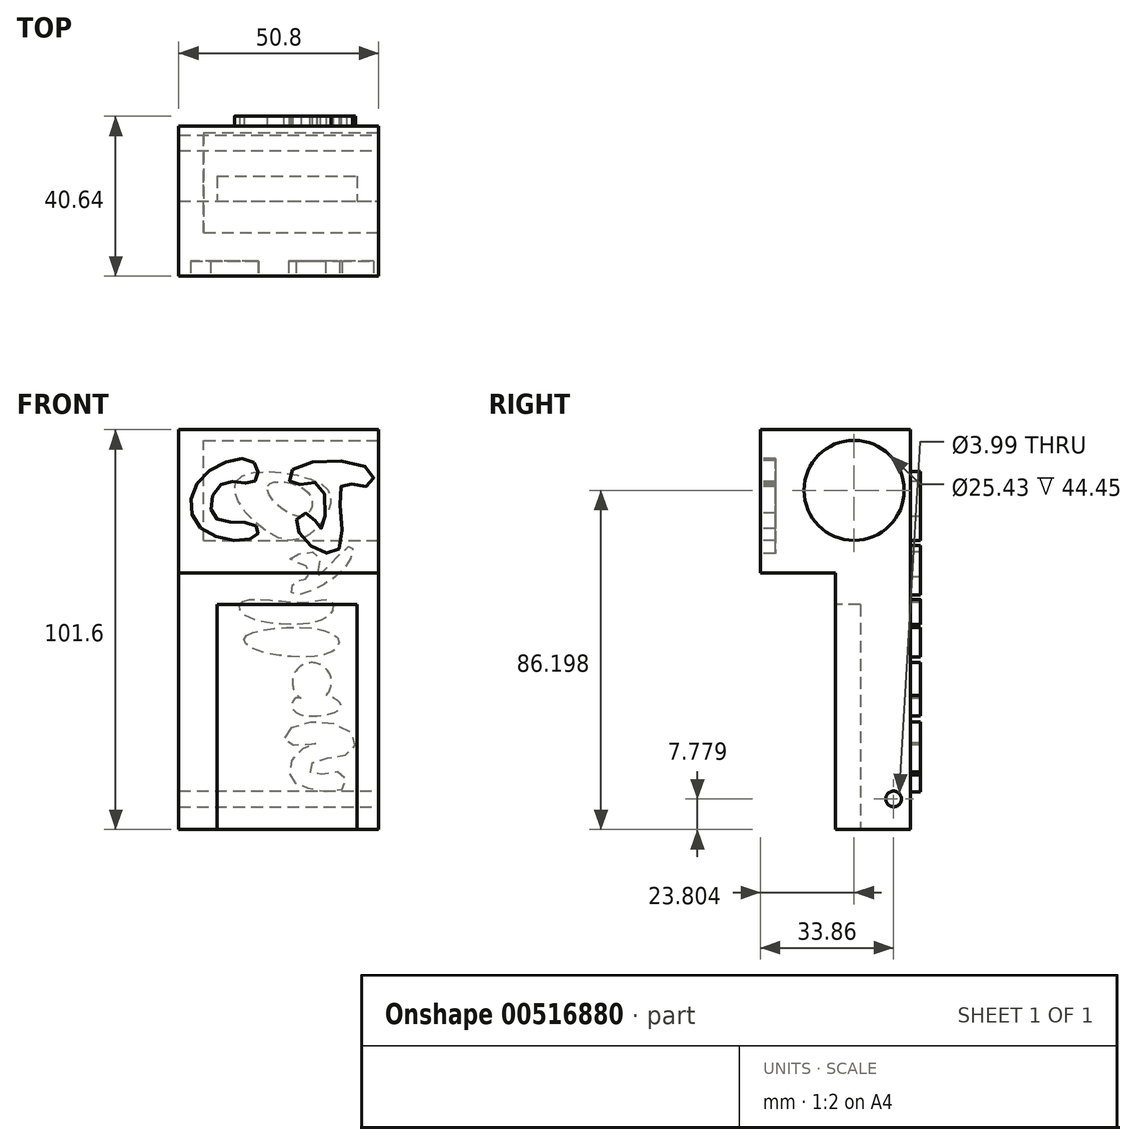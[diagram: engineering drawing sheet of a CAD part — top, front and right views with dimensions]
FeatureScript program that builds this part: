
annotation { "Feature Type Name" : "Feature", "Feature Type Description" : "" }
export const myFeature = defineFeature(function(context is Context, id is Id, definition is map)
    precondition{}
    {
        {
            var Q0;
            Q0=qCreatedBy(makeId("Front.planeOp"),FACE);
            var sketch = newSketch(context, id + "F0", { "sketchPlane" : qUnion([Q0])});
            skLineSegment(sketch, "E0.bottom", {"start": v(-43.59, 59.9) * mm, "end": v(7.21, 59.9) * mm});
            skLineSegment(sketch, "E0.top", {"start": v(-43.59, -41.7) * mm, "end": v(7.21, -41.7) * mm});
            skLineSegment(sketch, "E0.left", {"start": v(-43.59, 59.9) * mm, "end": v(-43.59, -41.7) * mm});
            skLineSegment(sketch, "E0.right", {"start": v(7.21, 59.9) * mm, "end": v(7.21, -41.7) * mm});
            skSolve(sketch);
        }
        {
            var Q0;
            Q0=makeQuery(id+"F0.imprint","IMPRINT",FACE,{"disambiguationData":[TD([[makeQuery(id+"F0.imprint","IMPRINT",EDGE,{"derivedFrom":sQuery(id+"F0.wireOp",EDGE,"E0.bottom")}),-1.0]])]});
            extrude(context, id + "F1", {"entities" : qUnion([Q0]), "depth" : 38.1 * mm, "offsetDistance" : 25.4 * mm});
        }
        {
            var Q0;
            Q0=makeQuery(id+"F1.opExtrude","CAP_FACE",FACE,{"disambiguationData":[OSD([sQuery(id+"F0.wireOp",EDGE,"E0.bottom"),sQuery(id+"F0.wireOp",EDGE,"E0.top"),sQuery(id+"F0.wireOp",EDGE,"E0.left"),sQuery(id+"F0.wireOp",EDGE,"E0.right")])],"isStart":false});
            var sketch = newSketch(context, id + "F2", { "sketchPlane" : qUnion([Q0])});
            skLineSegment(sketch, "E1.bottom", {"start": v(-33.9, 15.45) * mm, "end": v(1.66, 15.45) * mm});
            skLineSegment(sketch, "E1.top", {"start": v(-33.9, -41.7) * mm, "end": v(1.66, -41.7) * mm});
            skLineSegment(sketch, "E1.left", {"start": v(-33.9, 15.45) * mm, "end": v(-33.9, -41.7) * mm});
            skLineSegment(sketch, "E1.right", {"start": v(1.66, 15.45) * mm, "end": v(1.66, -41.7) * mm});
            skSolve(sketch);
        }
        {
            var Q0;
            Q0=makeQuery(id+"F2.imprint","IMPRINT",FACE,{"disambiguationData":[TD([[makeQuery(id+"F2.imprint","IMPRINT",EDGE,{"derivedFrom":sQuery(id+"F2.wireOp",EDGE,"E1.bottom")}),-1.0]])]});
            extrude(context, id + "F3", {"entities" : qUnion([Q0]), "operationType" : NewBodyOperationType.REMOVE, "oppositeDirection" : true, "depth" : 25.4 * mm, "offsetDistance" : 25.4 * mm});
        }
        {
            var Q0;
            Q0=makeQuery(id+"F1.opExtrude","SWEPT_FACE",FACE,{"disambiguationData":[OSD([sQuery(id+"F0.wireOp",EDGE,"E0.right")])]});
            var sketch = newSketch(context, id + "F4", { "sketchPlane" : qUnion([Q0])});
            skCircle(sketch, "E2", {"center": v(-4.24, -33.92) * mm, "radius": 2 * mm});
            skSolve(sketch);
        }
        {
            var Q0;
            Q0=makeQuery(id+"F4.imprint","IMPRINT",FACE,{"disambiguationData":[TD([[makeQuery(id+"F4.imprint","IMPRINT",EDGE,{"derivedFrom":sQuery(id+"F4.wireOp",EDGE,"E2")}),1.0]])]});
            extrude(context, id + "F5", {"entities" : qUnion([Q0]), "operationType" : NewBodyOperationType.REMOVE, "endBound" : BoundingType.THROUGH_ALL, "oppositeDirection" : true, "depth" : 25.4 * mm, "offsetDistance" : 25.4 * mm});
        }
        {
            var Q0;
            Q0=makeQuery(id+"F1.opExtrude","SWEPT_FACE",FACE,{"disambiguationData":[OSD([sQuery(id+"F0.wireOp",EDGE,"E0.right")])]});
            var sketch = newSketch(context, id + "F6", { "sketchPlane" : qUnion([Q0])});
            skCircle(sketch, "E3", {"center": v(-14.3, 44.5) * mm, "radius": 12.71 * mm});
            skSolve(sketch);
        }
        {
            var Q0;
            Q0=makeQuery(id+"F1.opExtrude","CAP_FACE",FACE,{"disambiguationData":[OSD([sQuery(id+"F0.wireOp",EDGE,"E0.bottom"),sQuery(id+"F0.wireOp",EDGE,"E0.top"),sQuery(id+"F0.wireOp",EDGE,"E0.left"),sQuery(id+"F0.wireOp",EDGE,"E0.right")])],"isStart":false});
            var sketch = newSketch(context, id + "F7", { "sketchPlane" : qUnion([Q0])});
            skLineSegment(sketch, "E4", {"start": v(-43.59, 23.47) * mm, "end": v(7.21, 23.47) * mm});
            skSolve(sketch);
        }
        {
            var Q0;
            {var subQ2=sQuery(id+"F7.wireOp",EDGE,"E4");Q0=makeQuery(id+"F7.imprint","IMPRINT",FACE,{"disambiguationData":[TD([[makeQuery(id+"F7.imprint","IMPRINT",EDGE,{"derivedFrom":subQ2}),-1.0]])]});}
            extrude(context, id + "F8", {"entities" : qUnion([Q0]), "operationType" : NewBodyOperationType.REMOVE, "oppositeDirection" : true, "depth" : 19.05 * mm, "offsetDistance" : 25.4 * mm});
        }
        {
            var Q0;
            Q0=makeQuery(id+"F6.imprint","IMPRINT",FACE,{"disambiguationData":[TD([[makeQuery(id+"F6.imprint","IMPRINT",EDGE,{"derivedFrom":sQuery(id+"F6.wireOp",EDGE,"E3")}),1.0]])]});
            extrude(context, id + "F9", {"entities" : qUnion([Q0]), "operationType" : NewBodyOperationType.REMOVE, "oppositeDirection" : true, "depth" : 44.45 * mm, "offsetDistance" : 25.4 * mm});
        }
        {
            var Q0;
            Q0=makeQuery(id+"F1.opExtrude","CAP_FACE",FACE,{"disambiguationData":[OSD([sQuery(id+"F0.wireOp",EDGE,"E0.bottom"),sQuery(id+"F0.wireOp",EDGE,"E0.top"),sQuery(id+"F0.wireOp",EDGE,"E0.left"),sQuery(id+"F0.wireOp",EDGE,"E0.right")])],"isStart":false});
            var sketch = newSketch(context, id + "F10", { "sketchPlane" : qUnion([Q0])});
            skFitSpline(sketch, "E5", {"points": [v(-24.52, 51.62) * mm, v(-37.6, 47.93) * mm, v(-38.16, 35.03) * mm, v(-23.97, 32.82) * mm, v(-24.52, 35.76) * mm, v(-34.66, 37.8) * mm, v(-32.45, 46.27) * mm, v(-24.52, 46.64) * mm, v(-24.52, 51.62) * mm]});
            skFitSpline(sketch, "E6", {"points": [v(-13.27, 49.78) * mm, v(-13.46, 46.46) * mm, v(-6.45, 45.9) * mm, v(-7.74, 35.03) * mm, v(-10.14, 37.8) * mm, v(-13.27, 37.98) * mm, v(-10.88, 30.6) * mm, v(-4.42, 30.79) * mm, v(-1.84, 45.9) * mm, v(4.6, 45.9) * mm, v(4.98, 49.6) * mm, v(-13.27, 49.78) * mm]});
            skSolve(sketch);
        }
        {
            var Q0;
            Q0=makeQuery(id+"F10.imprint","IMPRINT",FACE,{"disambiguationData":[TD([[makeQuery(id+"F10.imprint","IMPRINT",EDGE,{"derivedFrom":sQuery(id+"F10.wireOp",EDGE,"E5")}),1.0]])]});
            extrude(context, id + "F11", {"entities" : qUnion([Q0]), "operationType" : NewBodyOperationType.REMOVE, "oppositeDirection" : true, "depth" : 3.8 * mm, "offsetDistance" : 25.4 * mm});
        }
        {
            var Q0;
            Q0=makeQuery(id+"F1.opExtrude","CAP_FACE",FACE,{"disambiguationData":[OSD([sQuery(id+"F0.wireOp",EDGE,"E0.bottom"),sQuery(id+"F0.wireOp",EDGE,"E0.top"),sQuery(id+"F0.wireOp",EDGE,"E0.left"),sQuery(id+"F0.wireOp",EDGE,"E0.right")])],"isStart":false});
            var sketch = newSketch(context, id + "F12", { "sketchPlane" : qUnion([Q0])});
            skFitSpline(sketch, "E7", {"points": [v(-14.75, 49.78) * mm, v(-14.56, 46.09) * mm, v(-7.56, 45.72) * mm, v(-7.37, 34.84) * mm, v(-10.14, 38.35) * mm, v(-13.64, 37.06) * mm, v(-9.03, 29.68) * mm, v(-2.58, 30.23) * mm, v(-2.03, 45.9) * mm, v(4.24, 45.54) * mm, v(5.16, 49.6) * mm, v(-14.75, 49.78) * mm]});
            skSolve(sketch);
        }
        {
            var Q0;
            Q0=makeQuery(id+"F12.imprint","IMPRINT",FACE,{"disambiguationData":[TD([[makeQuery(id+"F12.imprint","IMPRINT",EDGE,{"derivedFrom":sQuery(id+"F12.wireOp",EDGE,"E7")}),1.0]])]});
            extrude(context, id + "F13", {"entities" : qUnion([Q0]), "operationType" : NewBodyOperationType.REMOVE, "oppositeDirection" : true, "depth" : 3.8 * mm, "offsetDistance" : 25.4 * mm});
        }
        {
            var Q0;
            Q0=makeQuery(id+"F1.opExtrude","CAP_FACE",FACE,{"disambiguationData":[OSD([sQuery(id+"F0.wireOp",EDGE,"E0.bottom"),sQuery(id+"F0.wireOp",EDGE,"E0.top"),sQuery(id+"F0.wireOp",EDGE,"E0.left"),sQuery(id+"F0.wireOp",EDGE,"E0.right")])],"isStart":true});
            var sketch = newSketch(context, id + "F14", { "sketchPlane" : qUnion([Q0])});
            skFitSpline(sketch, "E8", {"points": [v(29.13, 46.64) * mm, v(7.37, 46.09) * mm, v(5.72, 39.08) * mm, v(16.4, 31.9) * mm, v(29.13, 46.64) * mm]});
            skFitSpline(sketch, "E9", {"points": [v(21.02, 45.54) * mm, v(10.5, 43.7) * mm, v(12.54, 37.8) * mm, v(21.02, 45.54) * mm]});
            skFitSpline(sketch, "E10", {"points": [v(15.3, 27.1) * mm, v(8.11, 28.2) * mm, v(8.48, 22.5) * mm, v(0, 30.42) * mm, v(0, 27.1) * mm, v(6.64, 20.65) * mm, v(14.75, 18.25) * mm, v(14.01, 21.2) * mm, v(11.06, 22.12) * mm, v(11.06, 25.07) * mm, v(15.3, 27.1) * mm]});
            skFitSpline(sketch, "E11", {"points": [v(27.28, 16.22) * mm, v(11.43, 16.04) * mm, v(4.98, 16.4) * mm, v(5.72, 12.35) * mm, v(27.1, 12.9) * mm, v(27.28, 16.22) * mm]});
            skFitSpline(sketch, "E12", {"points": [v(26.36, 7.56) * mm, v(4.24, 7.93) * mm, v(4.24, 3.69) * mm, v(25.07, 4.42) * mm, v(26.36, 7.56) * mm]});
            skFitSpline(sketch, "E13", {"points": [v(13.09, -3.32) * mm, v(10.32, 0) * mm, v(5.53, -1.47) * mm, v(6.45, -7.56) * mm, v(11.43, -8.48) * mm, v(13.09, -3.32) * mm]});
            skFitSpline(sketch, "E14", {"points": [v(11.43, -8.48) * mm, v(14.2, -8.48) * mm, v(13.83, -11.98) * mm, v(2.4, -10.7) * mm, v(6.45, -7.56) * mm, v(11.43, -8.48) * mm]});
            skFitSpline(sketch, "E15", {"points": [v(15.12, -15.85) * mm, v(16.22, -19.73) * mm, v(8.48, -19.73) * mm, v(13.27, -21.94) * mm, v(15.3, -28.2) * mm, v(11.43, -30.97) * mm, v(1.66, -31.16) * mm, v(2.21, -27.28) * mm, v(9.59, -27.65) * mm, v(9.59, -24.7) * mm, v(0, -22.12) * mm, v(0, -16.78) * mm, v(15.12, -15.85) * mm]});
            skFitSpline(sketch, "E16", {"points": [v(9.77, -3.5) * mm, v(8.3, -2.21) * mm, v(7.37, -3.32) * mm, v(6.45, -5.53) * mm, v(9.03, -7.56) * mm, v(9.77, -3.5) * mm]});
            skSolve(sketch);
        }
        {
            var Q0;
            Q0=makeQuery(id+"F14.imprint","IMPRINT",FACE,{"disambiguationData":[TD([[makeQuery(id+"F14.imprint","IMPRINT",EDGE,{"derivedFrom":sQuery(id+"F14.wireOp",EDGE,"E8")}),1.0]])]});
            var Q1;
            Q1=makeQuery(id+"F14.imprint","IMPRINT",FACE,{"disambiguationData":[TD([[makeQuery(id+"F14.imprint","IMPRINT",EDGE,{"derivedFrom":sQuery(id+"F14.wireOp",EDGE,"E10")}),1.0]])]});
            var Q2;
            Q2=makeQuery(id+"F14.imprint","IMPRINT",FACE,{"disambiguationData":[TD([[makeQuery(id+"F14.imprint","IMPRINT",EDGE,{"derivedFrom":sQuery(id+"F14.wireOp",EDGE,"E11")}),1.0]])]});
            var Q3;
            Q3=makeQuery(id+"F14.imprint","IMPRINT",FACE,{"disambiguationData":[TD([[makeQuery(id+"F14.imprint","IMPRINT",EDGE,{"derivedFrom":sQuery(id+"F14.wireOp",EDGE,"E12")}),1.0]])]});
            var Q4;
            {var subQ0=sQuery(id+"F14.wireOp",EDGE,"E14");var subQ1=sQuery(id+"F14.wireOp",EDGE,"E13");var subQ2=makeQuery(id+"F14.imprint","INTERSECT",VERTEX,{"disambiguationData":[OD(0.0)],"derivedFrom":[subQ1,subQ0]});Q4=makeQuery(id+"F14.imprint","IMPRINT",FACE,{"disambiguationData":[TD([[makeQuery(id+"F14.imprint","IMPRINT",EDGE,{"disambiguationData":[TD([[subQ2,1.0]])],"derivedFrom":subQ1}),-1.0]])]});}
            var Q5;
            Q5=makeQuery(id+"F14.imprint","IMPRINT",FACE,{"disambiguationData":[TD([[makeQuery(id+"F14.imprint","IMPRINT",EDGE,{"derivedFrom":sQuery(id+"F14.wireOp",EDGE,"E15")}),-1.0]])]});
            extrude(context, id + "F15", {"entities" : qUnion([Q0, Q1, Q2, Q3, Q4, Q5]), "operationType" : NewBodyOperationType.ADD, "depth" : 2.54 * mm, "offsetDistance" : 25.4 * mm});
        }
        {
            var Q0;
            {var subQ0=sQuery(id+"F0.wireOp",EDGE,"E0.bottom");var subQ1=sQuery(id+"F0.wireOp",EDGE,"E0.top");var subQ2=sQuery(id+"F0.wireOp",EDGE,"E0.right");var subQ3=sQuery(id+"F0.wireOp",EDGE,"E0.left");Q0=makeQuery(id+"F15.boolean.opBoolean","SPLIT",FACE,{"disambiguationData":[TD([makeQuery(id+"F1.opExtrude","SWEPT_FACE",FACE,{"disambiguationData":[OSD([subQ0])]})])],"derivedFrom":makeQuery(id+"F1.opExtrude","CAP_FACE",FACE,{"disambiguationData":[OSD([subQ0,subQ1,subQ3,subQ2])],"isStart":true})});}
            var sketch = newSketch(context, id + "F16", { "sketchPlane" : qUnion([Q0])});
            skCircle(sketch, "E17", {"center": v(9.77, -4.24) * mm, "radius": 4.96 * mm});
            skSolve(sketch);
        }
        {
            var Q0;
            {var subQ4=makeQuery(id+"F15.opExtrude","CAP_EDGE",EDGE,{"disambiguationData":[OSD([sQuery(id+"F14.wireOp",EDGE,"E13")])],"isStart":true});Q0=makeQuery(id+"F16.imprint","IMPRINT",FACE,{"disambiguationData":[TD([[makeQuery(id+"F16.imprint","IMPRINT",EDGE,{"derivedFrom":subQ4}),1.0]])]});}
            extrude(context, id + "F17", {"entities" : qUnion([Q0]), "operationType" : NewBodyOperationType.ADD, "depth" : 2.54 * mm, "offsetDistance" : 25.4 * mm});
        }
    });
